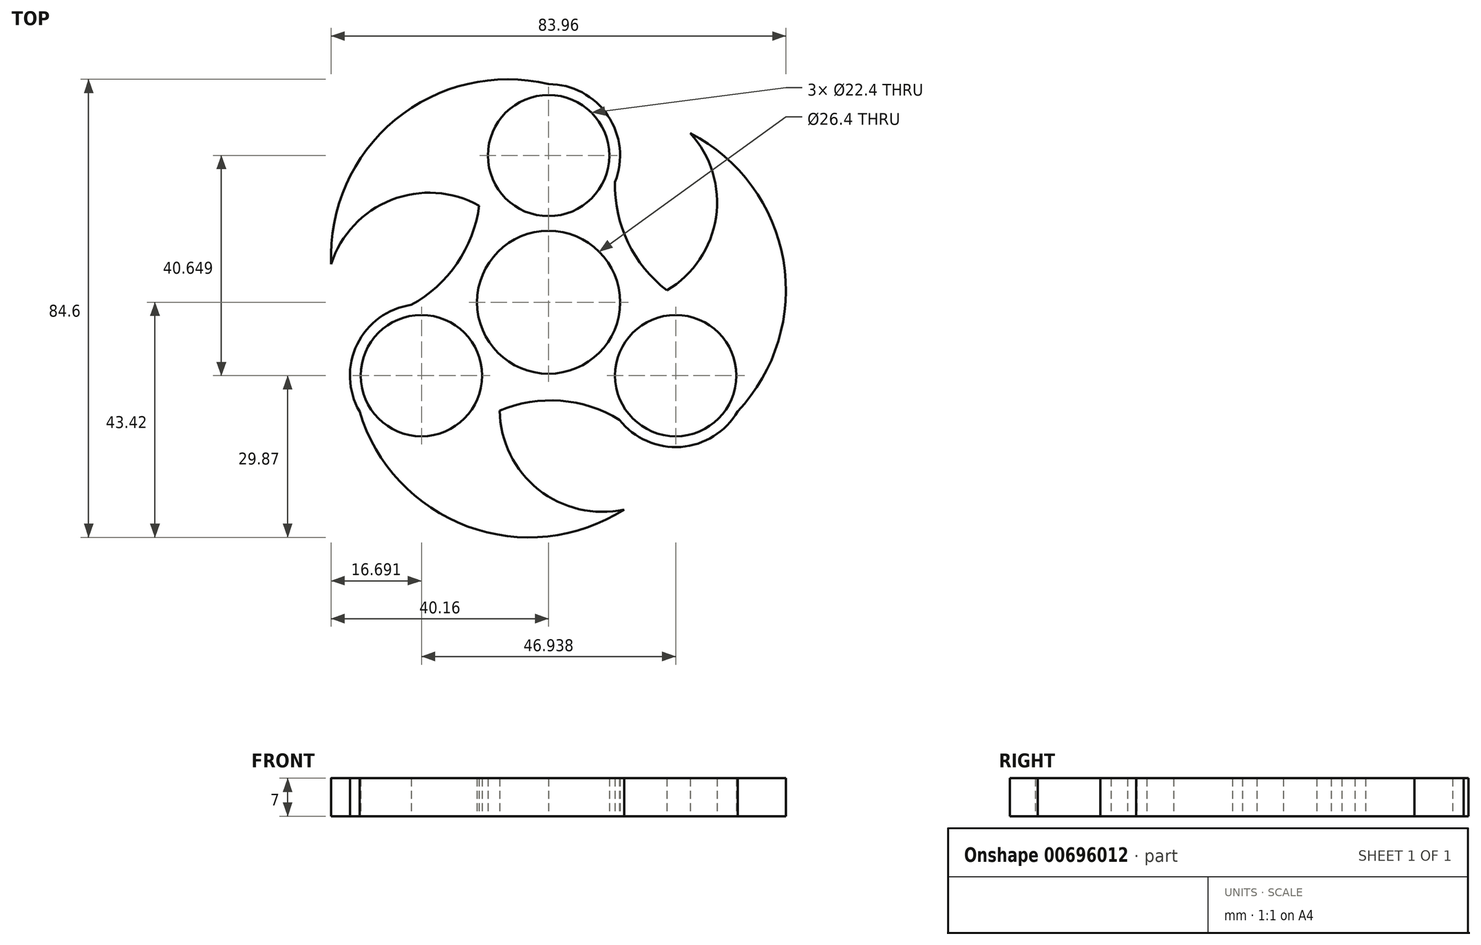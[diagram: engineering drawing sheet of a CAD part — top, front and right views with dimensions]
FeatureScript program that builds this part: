
annotation { "Feature Type Name" : "Feature", "Feature Type Description" : "" }
export const myFeature = defineFeature(function(context is Context, id is Id, definition is map)
    precondition{}
    {
        {
            var Q0;
            Q0=qCreatedBy(makeId("Top.planeOp"),FACE);
            var sketch = newSketch(context, id + "F0", { "sketchPlane" : qUnion([Q0])});
            skCircle(sketch, "E0", {"center": v(0, 0) * mm, "radius": 11.2 * mm});
            skCircle(sketch, "E1", {"center": v(0, 0) * mm, "radius": 13.2 * mm});
            skCircle(sketch, "E2", {"center": v(0, 27.1) * mm, "radius": 11.2 * mm});
            skArc(sketch, "E3", {"start": v(12.25, 22.2) * mm, "mid": v(0.94, 40.27) * mm, "end": v(-12.83, 23.99) * mm});
            skCircle(sketch, "E4.1.0", {"center": v(-23.47, -13.55) * mm, "radius": 11.2 * mm});
            skArc(sketch, "E4.1.1", {"start": v(-25.35, -0.48) * mm, "mid": v(-35.34, -19.32) * mm, "end": v(-14.36, -23.1) * mm});
            skCircle(sketch, "E4.2.0", {"center": v(23.47, -13.55) * mm, "radius": 11.2 * mm});
            skArc(sketch, "E4.2.1", {"start": v(13.1, -21.71) * mm, "mid": v(34.4, -20.95) * mm, "end": v(27.19, -0.88) * mm});
            skArc(sketch, "E5", {"start": v(-25.35, -0.48) * mm, "mid": v(-15.3, 9.82) * mm, "end": v(-12.83, 23.99) * mm});
            skArc(sketch, "E6.1.0", {"start": v(13.1, -21.71) * mm, "mid": v(-0.85, -18.16) * mm, "end": v(-14.36, -23.1) * mm});
            skArc(sketch, "E6.2.0", {"start": v(12.25, 22.2) * mm, "mid": v(16.15, 8.35) * mm, "end": v(27.19, -0.88) * mm});
            skPoint(sketch, "E7.orphan", {"position": v(-21.59, -0.48) * mm});
            skArc(sketch, "E8", {"start": v(0, 40.3) * mm, "mid": v(-28.34, 33.68) * mm, "end": v(-40.13, 7.06) * mm});
            skArc(sketch, "E9", {"start": v(-12.83, 17.84) * mm, "mid": v(-29.03, 18.9) * mm, "end": v(-40.13, 7.06) * mm});
            skArc(sketch, "E10.1.0", {"start": v(-34.9, -20.15) * mm, "mid": v(-15, -41.38) * mm, "end": v(13.95, -38.28) * mm});
            skArc(sketch, "E10.1.1", {"start": v(-9.03, -20.03) * mm, "mid": v(-1.86, -34.6) * mm, "end": v(13.95, -38.28) * mm});
            skArc(sketch, "E10.2.0", {"start": v(34.9, -20.15) * mm, "mid": v(43.34, 7.7) * mm, "end": v(26.18, 31.22) * mm});
            skArc(sketch, "E10.2.1", {"start": v(21.86, 2.2) * mm, "mid": v(30.89, 15.68) * mm, "end": v(26.18, 31.22) * mm});
            skSolve(sketch);
        }
        {
            var Q0;
            Q0 = qSketchRegion(id + "F0", true);
            extrude(context, id + "F1", {"entities" : qUnion([Q0]), "depth" : 7 * mm, "offsetDistance" : 25 * mm});
        }
    });
